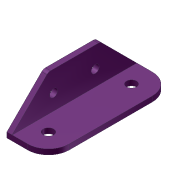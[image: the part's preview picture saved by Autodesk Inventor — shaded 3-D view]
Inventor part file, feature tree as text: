
AUTODESK INVENTOR PART (.ipt)
format: ipt  version: 2012 (Build 160160000, 160)  size: 116,736 bytes
history: native  units: in
note: dims shown in document units (in); Inventor stores cm internally (conversion verified against a paired STEP export)
features: extrude x3, sketch x3, fillet x2, chamfer x1
ambient origin geometry x8: Origin, YZ Plane, XZ Plane, XY Plane, X Axis, Y Axis, Z Axis, Center Point
bodies: Solid1 (feature_tree)
feature tree (9):
  extrude  "Extrusion1"  Depth=1.0in
  extrude  "Extrusion2"  Depth=1.0in
  extrude  "Extrusion3"  Depth=4.0in TaperAngle=0.0deg
  chamfer  "Chamfer1"  Distance=0.25in
  fillet  "Fillet1"  Radius=0.5in
  fillet  "Fillet2"  Radius=4.0in
  sketch  "Sketch1"  dims[d0=0.125in d1=1.0in]
  sketch  "Sketch2"  dims[d2=3.0in d3=0.0in d4=1.0in]
  sketch  "Sketch3"  dims[d5=0.192in d6=4.0in d7=0.0in d8=0.25in d9=0.5in d10=4.0in d11=0.0in d12=0.875in d13=0.125in d14=45.0deg d15=0.5in d16=0.125in]
